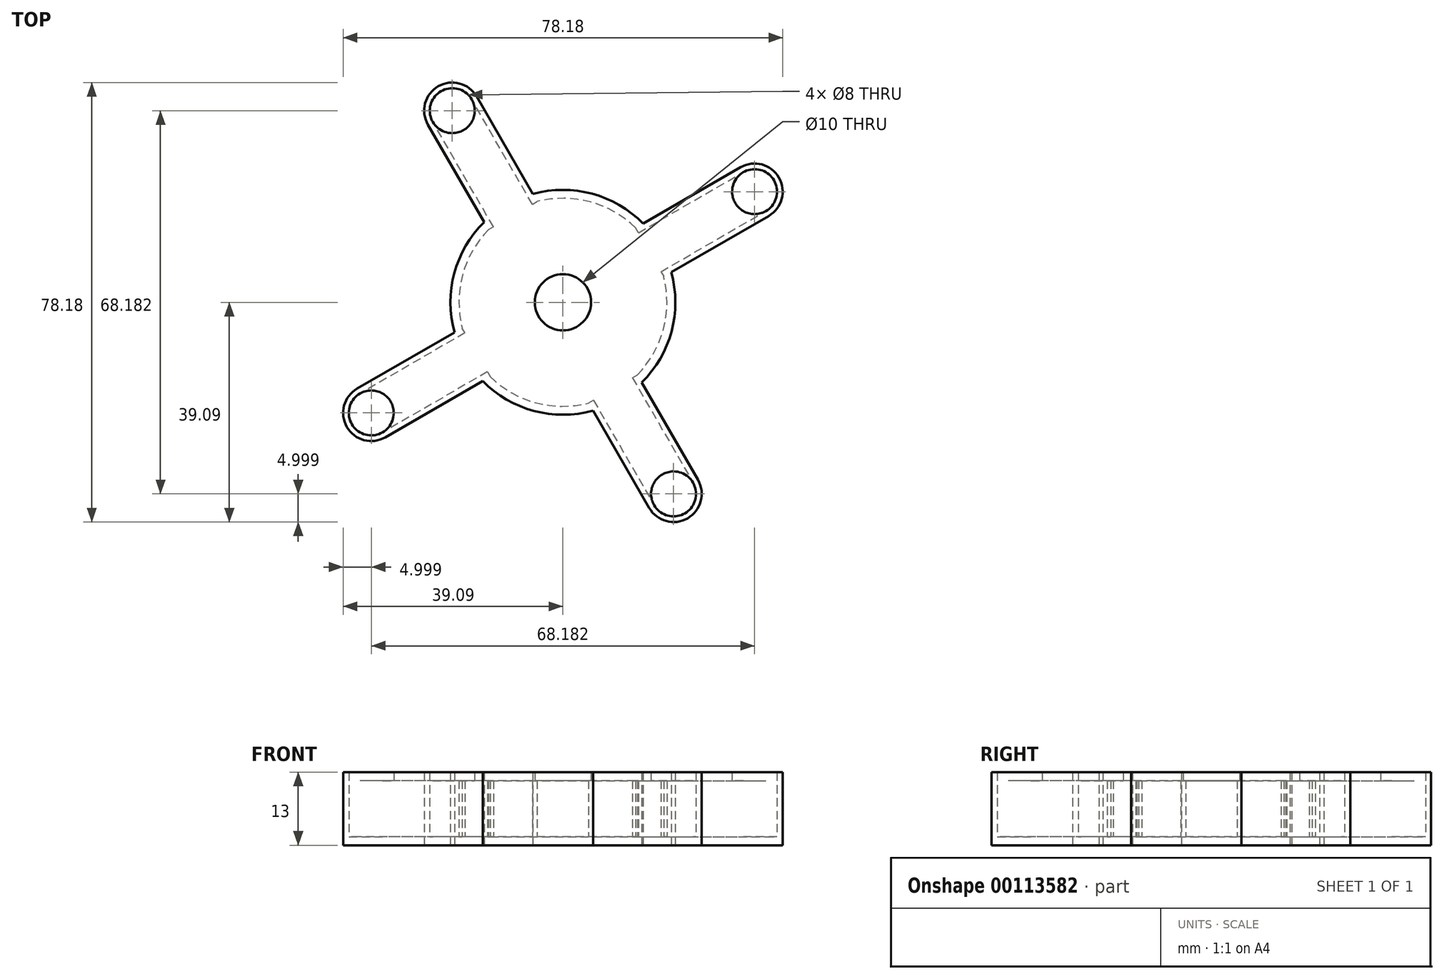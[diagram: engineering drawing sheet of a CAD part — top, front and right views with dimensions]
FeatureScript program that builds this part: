
annotation { "Feature Type Name" : "Feature", "Feature Type Description" : "" }
export const myFeature = defineFeature(function(context is Context, id is Id, definition is map)
    precondition{}
    {
        {
            var Q0;
            Q0=qCreatedBy(makeId("Top.planeOp"),FACE);
            var sketch = newSketch(context, id + "F0", { "sketchPlane" : qUnion([Q0])});
            skLineSegment(sketch, "E0", {"start": v(0, 0) * mm, "end": v(-53.86, -31.1) * mm, "construction": true});
            skArc(sketch, "E1", {"start": v(-20, 0) * mm, "mid": v(-19.82, -2.7) * mm, "end": v(-19.27, -5.35) * mm});
            skArc(sketch, "E2", {"start": v(-18.5, 0) * mm, "mid": v(-18.36, -2.3) * mm, "end": v(-17.93, -4.58) * mm});
            skLineSegment(sketch, "E3", {"start": v(-18.5, 0) * mm, "end": v(-20, 0) * mm});
            skLineSegment(sketch, "E4", {"start": v(0, -18.5) * mm, "end": v(0, -20) * mm});
            skLineSegment(sketch, "E5", {"start": v(-14.27, -14.01) * mm, "end": v(-31.6, -24.01) * mm});
            skLineSegment(sketch, "E6.MirrorCS", {"start": v(-19.27, -5.35) * mm, "end": v(-36.6, -15.35) * mm});
            skArc(sketch, "E7", {"start": v(-31.6, -24.01) * mm, "mid": v(-38.42, -22.18) * mm, "end": v(-36.6, -15.35) * mm});
            skArc(sketch, "E8.trimOffspring", {"start": v(-12.93, -13.24) * mm, "mid": v(-6.98, -17.13) * mm, "end": v(0, -18.5) * mm});
            skArc(sketch, "E9.trimOffspring", {"start": v(-14.27, -14.01) * mm, "mid": v(-7.74, -18.44) * mm, "end": v(0, -20) * mm});
            skLineSegment(sketch, "E10.0", {"start": v(-13.43, -12.37) * mm, "end": v(-32.1, -23.15) * mm});
            skArc(sketch, "E10.1", {"start": v(-32.1, -23.15) * mm, "mid": v(-37.56, -21.68) * mm, "end": v(-36.1, -16.22) * mm});
            skLineSegment(sketch, "E10.2", {"start": v(-17.43, -5.44) * mm, "end": v(-36.1, -16.22) * mm});
            skLineSegment(sketch, "E11", {"start": v(-13.43, -12.37) * mm, "end": v(-12.93, -13.24) * mm});
            skLineSegment(sketch, "E12", {"start": v(-17.43, -5.44) * mm, "end": v(-17.93, -4.58) * mm});
            skSolve(sketch);
        }
        {
            var Q0;
            Q0 = qSketchRegion(id + "F0", true);
            extrude(context, id + "F1", {"entities" : qUnion([Q0]), "depth" : 10 * mm});
        }
        {
            var Q0;
            Q0=qCreatedBy(makeId("Top.planeOp"),FACE);
            var sketch = newSketch(context, id + "F2", { "sketchPlane" : qUnion([Q0])});
            skArc(sketch, "E13.0", {"start": v(-20, 0) * mm, "mid": v(-19.82, -2.7) * mm, "end": v(-19.27, -5.35) * mm});
            skLineSegment(sketch, "E13.1", {"start": v(-19.27, -5.35) * mm, "end": v(-36.6, -15.35) * mm});
            skArc(sketch, "E13.2", {"start": v(-31.6, -24.01) * mm, "mid": v(-38.42, -22.18) * mm, "end": v(-36.6, -15.35) * mm});
            skLineSegment(sketch, "E13.3", {"start": v(-14.27, -14.01) * mm, "end": v(-31.6, -24.01) * mm});
            skArc(sketch, "E13.4", {"start": v(-14.27, -14.01) * mm, "mid": v(-7.74, -18.44) * mm, "end": v(0, -20) * mm});
            skLineSegment(sketch, "E14", {"start": v(-20, 0) * mm, "end": v(0, 0) * mm});
            skLineSegment(sketch, "E15", {"start": v(0, -20) * mm, "end": v(0, 0) * mm});
            skSolve(sketch);
        }
        {
            var Q0;
            Q0 = qSketchRegion(id + "F2", true);
            extrude(context, id + "F3", {"entities" : qUnion([Q0]), "operationType" : NewBodyOperationType.ADD, "oppositeDirection" : true, "depth" : 1.5 * mm});
        }
        {
            var Q0;
            Q0=makeQuery(id+"F1.opExtrude","CAP_FACE",FACE,{"disambiguationData":[OSD([sQuery(id+"F0.wireOp",EDGE,"E1"),sQuery(id+"F0.wireOp",EDGE,"E2"),sQuery(id+"F0.wireOp",EDGE,"E3"),sQuery(id+"F0.wireOp",EDGE,"E4"),sQuery(id+"F0.wireOp",EDGE,"E5"),sQuery(id+"F0.wireOp",EDGE,"E6.MirrorCS"),sQuery(id+"F0.wireOp",EDGE,"E7"),sQuery(id+"F0.wireOp",EDGE,"E8.trimOffspring"),sQuery(id+"F0.wireOp",EDGE,"E9.trimOffspring"),sQuery(id+"F0.wireOp",EDGE,"E10.0"),sQuery(id+"F0.wireOp",EDGE,"E10.1"),sQuery(id+"F0.wireOp",EDGE,"E10.2"),sQuery(id+"F0.wireOp",EDGE,"E11"),sQuery(id+"F0.wireOp",EDGE,"E12")])],"isStart":false});
            var sketch = newSketch(context, id + "F4", { "sketchPlane" : qUnion([Q0])});
            skArc(sketch, "E16.0", {"start": v(-20, 0) * mm, "mid": v(-19.82, -2.7) * mm, "end": v(-19.27, -5.35) * mm});
            skLineSegment(sketch, "E16.1", {"start": v(-19.27, -5.35) * mm, "end": v(-36.6, -15.35) * mm});
            skArc(sketch, "E16.2", {"start": v(-31.6, -24.01) * mm, "mid": v(-38.42, -22.18) * mm, "end": v(-36.6, -15.35) * mm});
            skLineSegment(sketch, "E16.3", {"start": v(-14.27, -14.01) * mm, "end": v(-31.6, -24.01) * mm});
            skArc(sketch, "E16.4", {"start": v(-14.27, -14.01) * mm, "mid": v(-7.74, -18.44) * mm, "end": v(0, -20) * mm});
            skLineSegment(sketch, "E17", {"start": v(-20, 0) * mm, "end": v(-5, 0) * mm});
            skLineSegment(sketch, "E18", {"start": v(0, -20) * mm, "end": v(0, -5) * mm});
            skArc(sketch, "E19", {"start": v(-5, 0) * mm, "mid": v(-3.54, -3.54) * mm, "end": v(0, -5) * mm});
            skCircle(sketch, "E20", {"center": v(-34.1, -19.68) * mm, "radius": 4 * mm});
            skSolve(sketch);
        }
        {
            var Q0;
            Q0 = qSketchRegion(id + "F4", true);
            extrude(context, id + "F5", {"entities" : qUnion([Q0]), "operationType" : NewBodyOperationType.ADD, "depth" : 1.5 * mm});
        }
        {
            var Q0;
            Q0=makeQuery(id+"F1.opExtrude","SWEPT_BODY",BODY,{"disambiguationData":[OSD([sQuery(id+"F0.wireOp",EDGE,"E1"),sQuery(id+"F0.wireOp",EDGE,"E2"),sQuery(id+"F0.wireOp",EDGE,"E3"),sQuery(id+"F0.wireOp",EDGE,"E4"),sQuery(id+"F0.wireOp",EDGE,"E5"),sQuery(id+"F0.wireOp",EDGE,"E6.MirrorCS"),sQuery(id+"F0.wireOp",EDGE,"E7"),sQuery(id+"F0.wireOp",EDGE,"E8.trimOffspring"),sQuery(id+"F0.wireOp",EDGE,"E9.trimOffspring"),sQuery(id+"F0.wireOp",EDGE,"E10.0"),sQuery(id+"F0.wireOp",EDGE,"E10.1"),sQuery(id+"F0.wireOp",EDGE,"E10.2"),sQuery(id+"F0.wireOp",EDGE,"E11"),sQuery(id+"F0.wireOp",EDGE,"E12")])]});
            var Q1;
            Q1=makeQuery(id+"F1.opExtrude","SWEPT_FACE",FACE,{"disambiguationData":[OSD([sQuery(id+"F0.wireOp",EDGE,"E9.trimOffspring")])]});
            circularPattern(context, id + "F6", {"operationType" : NewBodyOperationType.ADD, "entities" : qUnion([Q0]), "axis" : qUnion([Q1]), "angle" : 360 * degree, "instanceCount" : 4, "equalSpace" : true});
        }
    });
